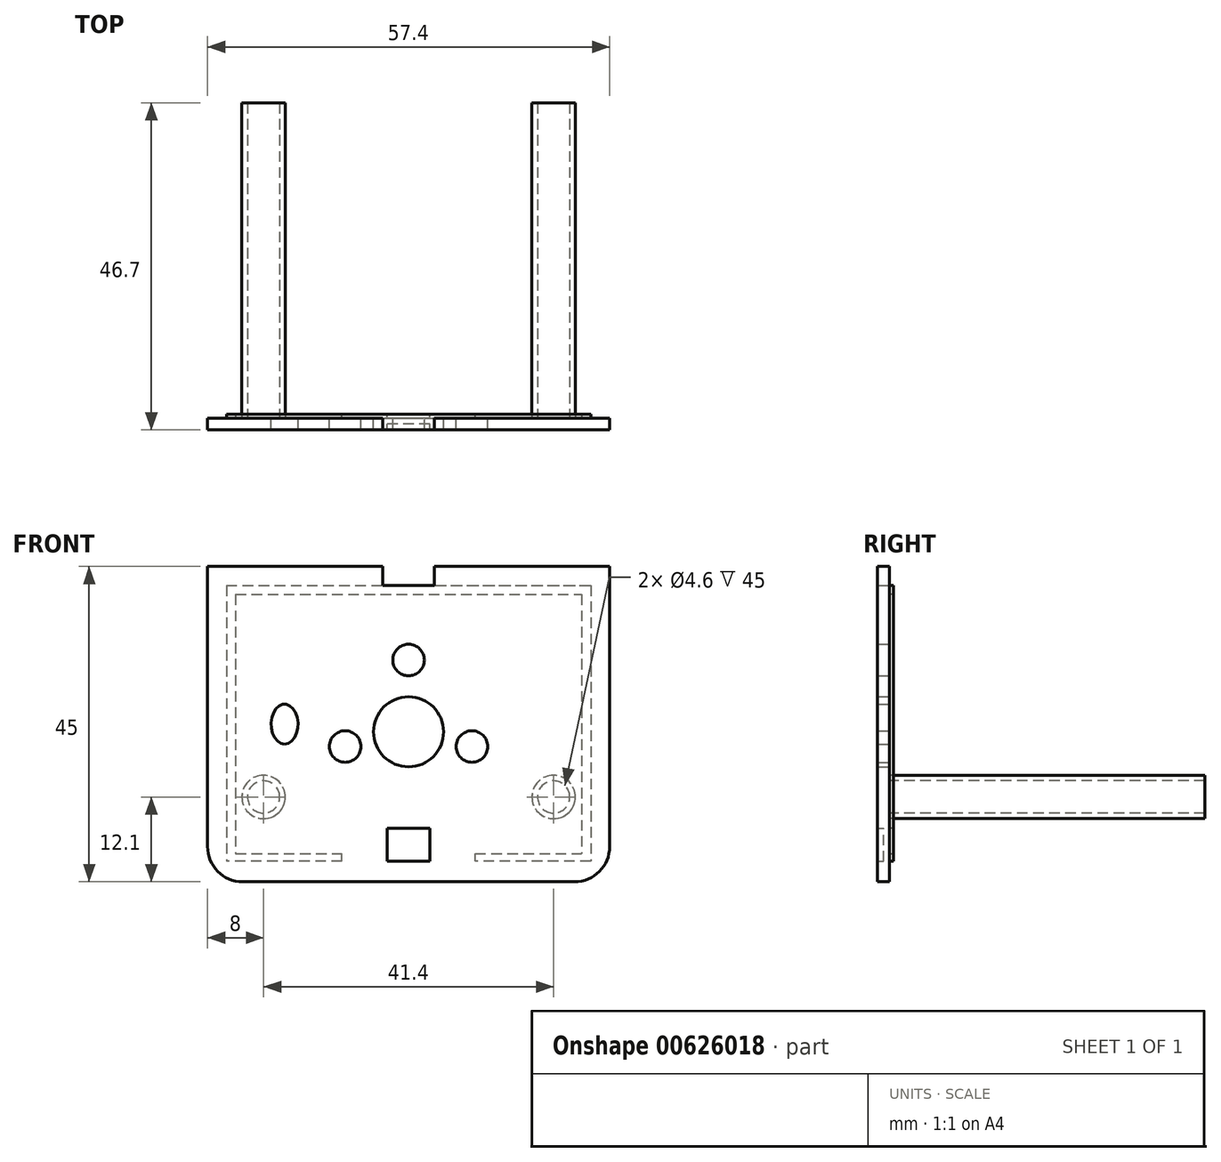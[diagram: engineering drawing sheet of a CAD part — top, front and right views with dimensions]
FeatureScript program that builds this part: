
annotation { "Feature Type Name" : "Feature", "Feature Type Description" : "" }
export const myFeature = defineFeature(function(context is Context, id is Id, definition is map)
    precondition{}
    {
        {
            var Q0;
            Q0=qCreatedBy(makeId("Front.planeOp"),FACE);
            var sketch = newSketch(context, id + "F0", { "sketchPlane" : qUnion([Q0])});
            skLineSegment(sketch, "E0.bottom", {"start": v(28.7, -22.5) * mm, "end": v(-28.7, -22.5) * mm});
            skLineSegment(sketch, "E0.top", {"start": v(28.7, 22.5) * mm, "end": v(-28.7, 22.5) * mm});
            skLineSegment(sketch, "E0.left", {"start": v(28.7, -22.5) * mm, "end": v(28.7, 22.5) * mm});
            skLineSegment(sketch, "E0.right", {"start": v(-28.7, -22.5) * mm, "end": v(-28.7, 22.5) * mm});
            skPoint(sketch, "E0.middle", {"position": v(0, 0) * mm});
            skCircle(sketch, "E1", {"center": v(0, -1.1) * mm, "radius": 5 * mm});
            skCircle(sketch, "E2", {"center": v(-9.05, -3.2) * mm, "radius": 2.25 * mm});
            skCircle(sketch, "E3", {"center": v(9.05, -3.2) * mm, "radius": 2.25 * mm});
            skCircle(sketch, "E4", {"center": v(0, 9.15) * mm, "radius": 2.25 * mm});
            skEllipse(sketch, "E5", {"center": v(-17.7, 0) * mm, "majorRadius": 2.85 * mm, "minorRadius": 1.92 * mm, "majorAxis": v(0, -1)});
            skLineSegment(sketch, "E6", {"start": v(-2.5, -14.9) * mm, "end": v(2.5, -14.9) * mm});
            skLineSegment(sketch, "E7", {"start": v(2.5, -14.9) * mm, "end": v(2.5, -14.9) * mm});
            skLineSegment(sketch, "E8", {"start": v(2.5, -14.9) * mm, "end": v(3.05, -14.9) * mm});
            skLineSegment(sketch, "E9", {"start": v(3.05, -14.9) * mm, "end": v(3.05, -19.6) * mm});
            skLineSegment(sketch, "E10", {"start": v(3.05, -19.6) * mm, "end": v(-3.05, -19.6) * mm});
            skLineSegment(sketch, "E11", {"start": v(-3.05, -19.6) * mm, "end": v(-3.05, -14.9) * mm});
            skLineSegment(sketch, "E12", {"start": v(-2.5, -14.9) * mm, "end": v(-2.5, -14.9) * mm});
            skLineSegment(sketch, "E13", {"start": v(-2.5, -14.9) * mm, "end": v(-3.05, -14.9) * mm});
            skPoint(sketch, "E14", {"position": v(0, -19.6) * mm});
            skLineSegment(sketch, "E15.bottom", {"start": v(3.7, 19.8) * mm, "end": v(-3.7, 19.8) * mm});
            skLineSegment(sketch, "E15.top", {"start": v(3.7, 25.2) * mm, "end": v(-3.7, 25.2) * mm});
            skLineSegment(sketch, "E15.left", {"start": v(3.7, 19.8) * mm, "end": v(3.7, 25.2) * mm});
            skLineSegment(sketch, "E15.right", {"start": v(-3.7, 19.8) * mm, "end": v(-3.7, 25.2) * mm});
            skPoint(sketch, "E15.middle", {"position": v(0, 22.5) * mm});
            skSolve(sketch);
        }
        {
            var Q0;
            Q0=makeQuery(id+"F0.imprint","IMPRINT",FACE,{"disambiguationData":[TD([[makeQuery(id+"F0.imprint","IMPRINT",EDGE,{"derivedFrom":sQuery(id+"F0.wireOp",EDGE,"E8")}),-1.0]])]});
            extrude(context, id + "F1", {"entities" : qUnion([Q0]), "oppositeDirection" : true, "depth" : 1.4 * mm, "offsetDistance" : 25 * mm});
        }
        {
            var Q0;
            Q0=makeQuery(id+"F0.imprint","IMPRINT",FACE,{"disambiguationData":[TD([[makeQuery(id+"F0.imprint","IMPRINT",EDGE,{"derivedFrom":sQuery(id+"F0.wireOp",EDGE,"E0.bottom")}),-1.0]])]});
            extrude(context, id + "F2", {"entities" : qUnion([Q0]), "operationType" : NewBodyOperationType.ADD, "depth" : 1.7 * mm, "offsetDistance" : 25 * mm, "symmetric" : true});
        }
        {
            var Q0;
            Q0=qCreatedBy(makeId("Front.planeOp"),FACE);
            var sketch = newSketch(context, id + "F3", { "sketchPlane" : qUnion([Q0])});
            skLineSegment(sketch, "E16.bottom", {"start": v(-26, 19.8) * mm, "end": v(26, 19.8) * mm});
            skLineSegment(sketch, "E16.top", {"start": v(-26, -19.6) * mm, "end": v(26, -19.6) * mm});
            skLineSegment(sketch, "E16.left", {"start": v(-26, 19.8) * mm, "end": v(-26, -19.6) * mm});
            skLineSegment(sketch, "E16.right", {"start": v(26, 19.8) * mm, "end": v(26, -19.6) * mm});
            skPoint(sketch, "E16.middle", {"position": v(0, 0.1) * mm});
            skLineSegment(sketch, "E17.bottom", {"start": v(-24.7, 18.5) * mm, "end": v(24.7, 18.5) * mm});
            skLineSegment(sketch, "E17.top", {"start": v(-24.7, -18.5) * mm, "end": v(24.7, -18.5) * mm});
            skLineSegment(sketch, "E17.left", {"start": v(-24.7, 18.5) * mm, "end": v(-24.7, -18.5) * mm});
            skLineSegment(sketch, "E17.right", {"start": v(24.7, 18.5) * mm, "end": v(24.7, -18.5) * mm});
            skPoint(sketch, "E17.middle", {"position": v(0, 0) * mm});
            skSolve(sketch);
        }
        {
            var Q0;
            Q0 = qSketchRegion(id + "F3", true);
            extrude(context, id + "F4", {"entities" : qUnion([Q0]), "operationType" : NewBodyOperationType.ADD, "oppositeDirection" : true, "depth" : 1.4 * mm, "offsetDistance" : 25 * mm});
        }
        {
            var Q0;
            Q0=makeQuery(id+"F4.boolean.opBoolean","MERGE",FACE,{"derivedFrom":[makeQuery(id+"F1.opExtrude","CAP_FACE",FACE,{"disambiguationData":[OSD([sQuery(id+"F0.wireOp",EDGE,"E8"),sQuery(id+"F0.wireOp",EDGE,"E9"),sQuery(id+"F0.wireOp",EDGE,"E10"),sQuery(id+"F0.wireOp",EDGE,"E11"),sQuery(id+"F0.wireOp",EDGE,"E13"),sQuery(id+"F0.wireOp",EDGE,"E6")])],"isStart":false}),makeQuery(id+"F4.opExtrude","CAP_FACE",FACE,{"disambiguationData":[OSD([sQuery(id+"F3.wireOp",EDGE,"E16.bottom"),sQuery(id+"F3.wireOp",EDGE,"E16.top"),sQuery(id+"F3.wireOp",EDGE,"E16.left"),sQuery(id+"F3.wireOp",EDGE,"E16.right"),sQuery(id+"F3.wireOp",EDGE,"E17.bottom"),sQuery(id+"F3.wireOp",EDGE,"E17.top"),sQuery(id+"F3.wireOp",EDGE,"E17.left"),sQuery(id+"F3.wireOp",EDGE,"E17.right")])],"isStart":false})]});
            var sketch = newSketch(context, id + "F5", { "sketchPlane" : qUnion([Q0])});
            skLineSegment(sketch, "E18", {"start": v(-9.5, -18.5) * mm, "end": v(-9.5, -19.6) * mm});
            skLineSegment(sketch, "E19", {"start": v(9.5, -18.5) * mm, "end": v(9.5, -19.6) * mm});
            skLineSegment(sketch, "E20", {"start": v(-3.05, -18.5) * mm, "end": v(-3.05, -19.6) * mm});
            skLineSegment(sketch, "E21", {"start": v(3.05, -18.5) * mm, "end": v(3.05, -19.6) * mm});
            skSolve(sketch);
        }
        {
            var Q0;
            {var subQ0=sQuery(id+"F0.wireOp",EDGE,"E7");var subQ1=sQuery(id+"F0.wireOp",EDGE,"E5");var subQ2=sQuery(id+"F0.wireOp",EDGE,"E2");var subQ3=sQuery(id+"F0.wireOp",EDGE,"E3");var subQ4=sQuery(id+"F0.wireOp",EDGE,"E13");var subQ5=sQuery(id+"F0.wireOp",EDGE,"E8");var subQ6=sQuery(id+"F0.wireOp",EDGE,"E4");var subQ7=sQuery(id+"F0.wireOp",EDGE,"E9");var subQ8=sQuery(id+"F0.wireOp",EDGE,"E1");var subQ9=sQuery(id+"F0.wireOp",EDGE,"E6");var subQ10=sQuery(id+"F0.wireOp",EDGE,"E11");var subQ11=sQuery(id+"F0.wireOp",EDGE,"E12");Q0=makeQuery(id+"F4.boolean.opBoolean","SPLIT",FACE,{"disambiguationData":[TD([makeQuery(id+"F1.opExtrude","SWEPT_FACE",FACE,{"disambiguationData":[OSD([subQ7])]})])],"derivedFrom":makeQuery(id+"F2.opExtrude","CAP_FACE",FACE,{"disambiguationData":[OSD([sQuery(id+"F0.wireOp",EDGE,"E0.bottom"),sQuery(id+"F0.wireOp",EDGE,"E0.top"),sQuery(id+"F0.wireOp",EDGE,"E0.left"),sQuery(id+"F0.wireOp",EDGE,"E0.right"),subQ8,subQ2,subQ3,subQ6,subQ1,subQ9,subQ0,subQ5,subQ7,sQuery(id+"F0.wireOp",EDGE,"E10"),subQ10,subQ11,subQ4,sQuery(id+"F0.wireOp",EDGE,"E15.bottom"),sQuery(id+"F0.wireOp",EDGE,"E15.left"),sQuery(id+"F0.wireOp",EDGE,"E15.right")])],"isStart":true})});}
            var sketch = newSketch(context, id + "F6", { "sketchPlane" : qUnion([Q0])});
            skCircle(sketch, "E22", {"center": v(-20.7, -10.4) * mm, "radius": 3.1 * mm});
            skCircle(sketch, "E23", {"center": v(20.7, -10.4) * mm, "radius": 3.1 * mm});
            skCircle(sketch, "E24", {"center": v(-20.7, -10.4) * mm, "radius": 2.3 * mm});
            skCircle(sketch, "E25", {"center": v(20.7, -10.4) * mm, "radius": 2.3 * mm});
            skSolve(sketch);
        }
        {
            var Q0;
            Q0=makeQuery(id+"F6.imprint","IMPRINT",FACE,{"disambiguationData":[TD([[makeQuery(id+"F6.imprint","IMPRINT",EDGE,{"derivedFrom":sQuery(id+"F6.wireOp",EDGE,"E22")}),1.0]])]});
            var Q1;
            Q1=makeQuery(id+"F6.imprint","IMPRINT",FACE,{"disambiguationData":[TD([[makeQuery(id+"F6.imprint","IMPRINT",EDGE,{"derivedFrom":sQuery(id+"F6.wireOp",EDGE,"E23")}),1.0]])]});
            extrude(context, id + "F7", {"entities" : qUnion([Q0, Q1]), "operationType" : NewBodyOperationType.ADD, "depth" : 45 * mm, "offsetDistance" : 25 * mm});
        }
        {
            var Q0;
            Q0=makeQuery(id+"F2.opExtrude","SWEPT_EDGE",EDGE,{"disambiguationData":[OSD([sQuery(id+"F0.wireOp",EDGE,"E0.bottom"),sQuery(id+"F0.wireOp",EDGE,"E0.left")])]});
            var Q1;
            Q1=makeQuery(id+"F2.opExtrude","SWEPT_EDGE",EDGE,{"disambiguationData":[OSD([sQuery(id+"F0.wireOp",EDGE,"E0.bottom"),sQuery(id+"F0.wireOp",EDGE,"E0.right")])]});
            fillet(context, id + "F8", {"entities" : qUnion([Q0, Q1]), "radius" : 5 * mm, "tangentPropagation" : true, "allowEdgeOverflow" : false});
        }
        {
            var Q0;
            {var subQ0=sQuery(id+"F5.wireOp",EDGE,"E18");Q0=makeQuery(id+"F5.imprint","IMPRINT",FACE,{"disambiguationData":[TD([[makeQuery(id+"F5.imprint","IMPRINT",EDGE,{"derivedFrom":subQ0}),1.0]])]});}
            var Q1;
            {var subQ0=sQuery(id+"F5.wireOp",EDGE,"E19");Q1=makeQuery(id+"F5.imprint","IMPRINT",FACE,{"disambiguationData":[TD([[makeQuery(id+"F5.imprint","IMPRINT",EDGE,{"derivedFrom":subQ0}),-1.0]])]});}
            extrude(context, id + "F9", {"entities" : qUnion([Q0, Q1]), "operationType" : NewBodyOperationType.REMOVE, "oppositeDirection" : true, "depth" : 1.1 * mm, "offsetDistance" : 25 * mm, "symmetric" : true});
        }
    });
